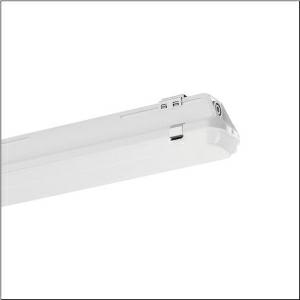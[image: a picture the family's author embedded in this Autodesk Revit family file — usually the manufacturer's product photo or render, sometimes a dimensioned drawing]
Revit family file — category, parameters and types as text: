
# Revit family: monsun_r__11_parking_51fg20dp440l_74b4
name_source: partatom
category: Lighting Fixtures
units: mm (PartAtom-declared; Revit-internal decimal feet)

## family parameters
Cut with Voids When Loaded = No
Host = Face
Light Source = No
Part Type = Normal
Room Calculation Point = No
Round Connector Dimension = Use Diameter
Shared = No

## types (1)
- --- (1 x LED, 4840 lm, 28.1 W, 4000K)
    Apparent Load = 28 VA
    CIE Flux Codes = 45 75 93 94 100
    Color Rendering = 80
    Color Temperature = 4000K
    Default Elevation = 1800 mm
    Description = Monsun® 11 parking, damp-proof luminaire, chain hanger, primary optical cover: enclosure, of PC, light emission: direct distribution, primary light characteristic: symmetric, installation type: suspended mounting, surface-mounted, horizontal mounting, vertical mounting, LED, rated luminous flux: 4.840lm, luminous efficacy: 172lm/W, light colour: 840, colour temperature: 4000K, control gear: DALI 2, with terminal, 5-pole, max. 2.5mm², mains connection: 220..240V, AC, 50/60Hz, rated input power: 28W, housing, of glass-fibre reinforced polyester, uncoated, bright grey, incl. chain hanger, length: 1.590mm, width: 90mm, height: 88mm, clip for enclosure, of stainless steel (V2A), ceiling mounting element, of stainless steel (V2A), chain hanger, of stainless steel (V2A), protection rating (complete): IP66, insulation class (complete): insulation class I (protective earthing), certification: CE, ENEC, VDE, UKCA, protection symbol: D, impact resistance: IK08, permissible operating ambient temperature: -25..+40°C, standard: EN 50419, EN 60598-2-1, corresponds to IFS (International Featured Standards) requirements for safety and quality in the food industry, for indoor or canopied outdoor use, no direct snow, no direct sun, no direct rain, LABS conformity tested according to VDMA 24364:2018-05, contact your sales advisor before using the luminaires in applications with unclear chemical exposure, large temperature fluctuations or condensation-forming humidity, packaging unit: 1 piece
    Height = 89 mm
    Lamp = 1 x LED
    Lamp Light Flux = 4840 lm
    Lamp Power = 28.1 W
    Lamp count = 1
    Length = 1590 mm
    Luminous efficacy = 172 lm/W
    Manufacturer = Siteco
    ModVariant = No
    Model = 51FG20DP440L
    Mounting Place = Ceiling
    Mounting Type = Surface mounted
    Number of Poles = 1
    OnlyDefault = Yes
    Power Factor = 1
    Product Name = Monsun® 11 parking
    Product group = damp-proof luminaire
    ProductGroupID = 300
    Protection Class = Protection class I
    Protection Degree = IP 66
    RLX_Detail_Level = 1
    RLX_Emergency_Light_Flux = 0 lm
    RLX_Emergency_Type = 0
    RLX_Emergency_Type_DB = No
    RlxData = <blob elided: 92209 chars, md5=9189ac7a>
    Socket = socket
    Standby Power = 0 W
    System Light Flux = 4840 lm
    System Power = 28 W
    Type Comments = factory setting: luminous flux: 100 % | dim-lin: 254 | 193 mA
    Type Image = l_1349237.jpg
    URL = http://relux.com
    VarID = @adj_017624
    Voltage = 0 V
    Weight = 0.00 kg
    Width = 90 mm

## geometry (parser evidence)
native form markers: Blend x4, Sweep x14
no freeform markers — native parametric forms only
